# Revit family: Emergency_Equipment-Haws_Corporation-Eye_Face_Wash_7360BTWC
name_source: partatom
category: Plumbing Fixtures
revit_build: Autodesk Revit 2016 (Build: 20150220_1215(x64)
units: mm (PartAtom-declared; Revit-internal decimal feet)

## family parameters
Always vertical = Yes
Cut with Voids When Loaded = No
Host = Wall
OmniClass Number = 23.45.05.14.24
OmniClass Title = Eye Wash Fountains
Part Type = Normal
Room Calculation Point = No
Round Connector Dimension = Use Radius
Shared = Yes

## types (1)
- 7360B-7460BTWC
    Assembly Code = D2010610
    BIMobject category = Other
    BIMobject category code = sanitary-sanitary-other
    BIMobject main category = Sanitary
    BIMobject main category code = sanitary
    Bowl = Metal - Haws Corporation - Green Powder Coating
    Bowl Diam. = 11"
    Bracket = Metal - Haws Corporation - Galvanized Steel
    Brand url = https://www.hawsco.com
    CW Connection = Yes
    CWFU = 1
    Cost = $0
    Cost Note = For Cost information please visit the Resource tab in the Product Page URL
    Date of publishing = 6/4/2019
    Description = Eyewash streams provide zero vertical velocity stream engineering with even laminar flow for enhanced comfort
    Design country = United States
    EAN code = https://611970347998
    Edition number = 1
    Flow = 3.70 GPM
    HW Connection = No
    HWFU = 0
    Head Level = 40"
    Installation instructions = http://www.hawsco.com
    Keynote = 15400
    Manufacturer = Haws Corporation 1455 Kleppe Lane Sparks, NV 89431
    Manufacturer country = United States
    Manufacturer name = Haws Corporation
    Masterformat 2014 Code = 22 45 26
    Masterformat 2014 Description = Eye/Face Wash Equipment
    Material main = Metal
    Model = 7360B-7460B
    Nominal height = 7"
    Nominal width = 19"
    OmniClass Code = 23-29 37 13 15
    OmniClass Description = Combination Emergency Eye Wash Stations
    Product Documentation Link = http://www.hawsco.com
    Product Guid = e264ad97-81b5-475a-8520-22a50c9a0c50
    Product Page URL = http://www.hawsco.com
    Product SKU = haws-7360b-7460b
    Product certification = http://www.csagroup.org
    Product data url = https://bimobject.com
    Product family = Eye Wash Fountains
    Product group = Emergency Equipment - Eye & Face Washes
    Product url = https://www.hawsco.com
    Sanitary Radius = 5/8"
    Series = AXION MSR™ Eye/Face Wash
    Supply Radius = 1/4"
    Technical description = http://www.hawsco.com
    Tubing = Metal - Haws Corporation - Smokey Pearl
    Type Comments = Features a round 11" stainless steel receptor and aluminum wall bracket for long life
    URL = http://www.hawsco.com
    Vent Connection = No
    WFU = 1
    Waste Connection = Yes
    Waste Level = 10 3/8"
    Weight Net (Kg) = 7

## geometry (parser evidence)
native form markers: Blend x12, Sweep x5
no freeform markers — native parametric forms only
